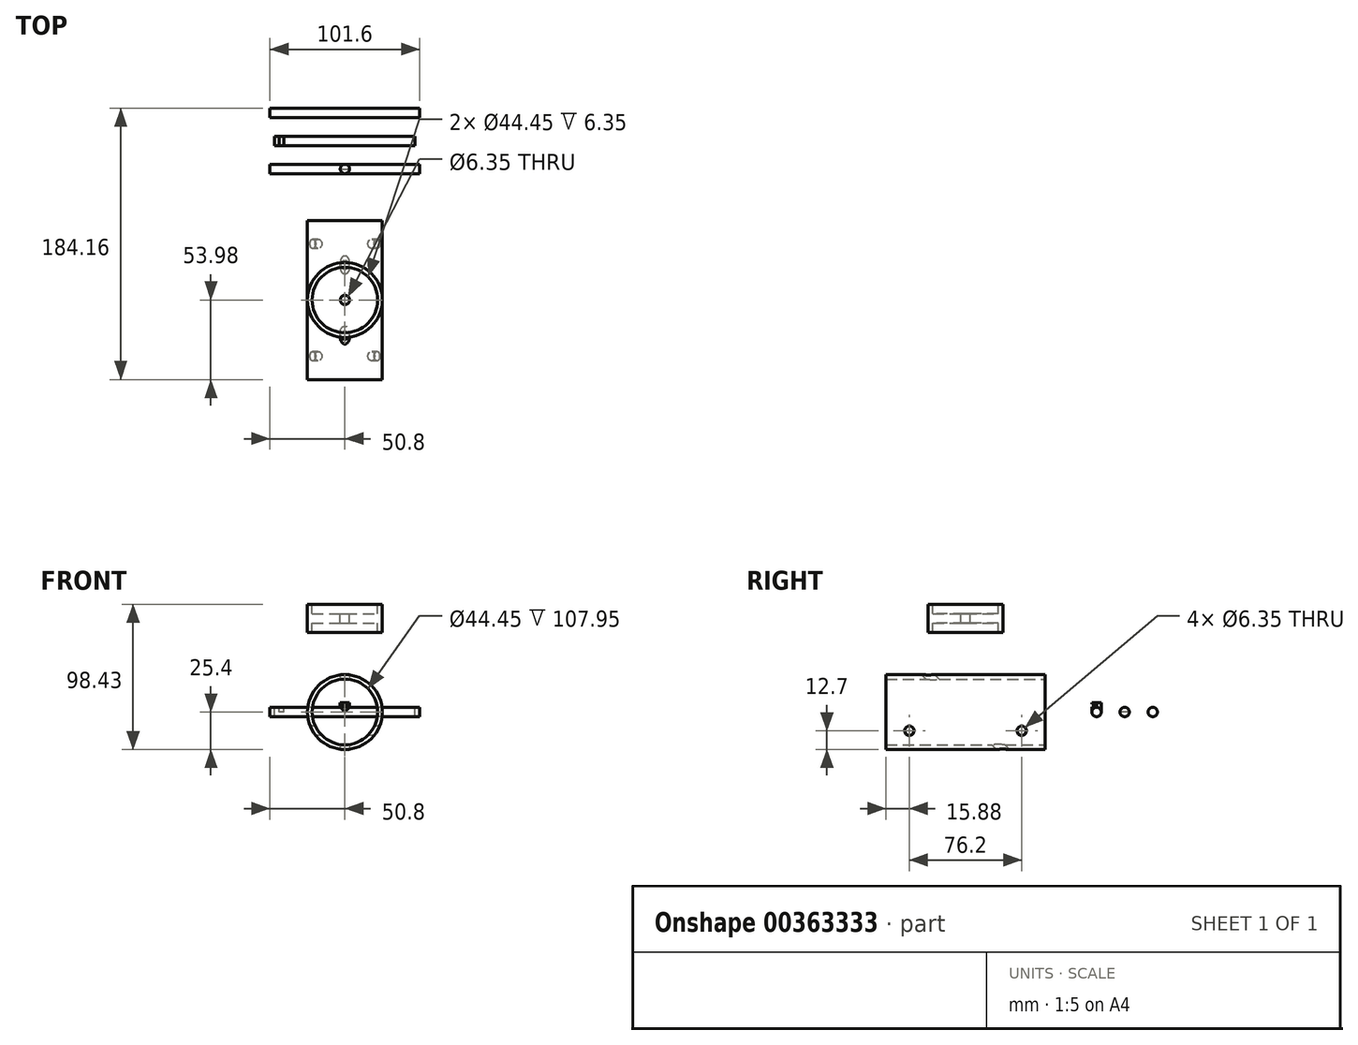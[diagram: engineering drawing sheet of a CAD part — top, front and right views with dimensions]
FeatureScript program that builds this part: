
annotation { "Feature Type Name" : "Feature", "Feature Type Description" : "" }
export const myFeature = defineFeature(function(context is Context, id is Id, definition is map)
    precondition{}
    {
        {
            var Q0;
            Q0=qCreatedBy(makeId("Front.planeOp"),FACE);
            var sketch = newSketch(context, id + "F0", { "sketchPlane" : qUnion([Q0])});
            skCircle(sketch, "E0", {"center": v(0, 0) * mm, "radius": 25.4 * mm});
            skCircle(sketch, "E1", {"center": v(0, 0) * mm, "radius": 22.23 * mm});
            skSolve(sketch);
        }
        {
            var Q0;
            Q0=makeQuery(id+"F0.imprint","IMPRINT",FACE,{"disambiguationData":[TD([[makeQuery(id+"F0.imprint","IMPRINT",EDGE,{"derivedFrom":sQuery(id+"F0.wireOp",EDGE,"E0")}),1.0]])]});
            var Q1;
            Q1=sQuery(id+"F0.wireOp",EDGE,"E0");
            extrude(context, id + "F1", {"entities" : qUnion([Q0]), "surfaceEntities" : qUnion([Q1]), "depth" : 107.95 * mm, "symmetric" : true});
        }
        {
            var Q0;
            Q0=qCreatedBy(makeId("Right.planeOp"),FACE);
            var sketch = newSketch(context, id + "F2", { "sketchPlane" : qUnion([Q0])});
            skLineSegment(sketch, "E2", {"start": v(0, 0) * mm, "end": v(-38.1, 0) * mm, "construction": true});
            skLineSegment(sketch, "E3", {"start": v(0, 0) * mm, "end": v(38.1, 0) * mm, "construction": true});
            skLineSegment(sketch, "E4", {"start": v(-38.1, 0) * mm, "end": v(-38.1, -12.7) * mm, "construction": true});
            skLineSegment(sketch, "E5", {"start": v(38.1, 0) * mm, "end": v(38.1, -12.7) * mm, "construction": true});
            skCircle(sketch, "E6", {"center": v(-38.1, -12.7) * mm, "radius": 3.18 * mm});
            skCircle(sketch, "E7", {"center": v(38.1, -12.7) * mm, "radius": 3.18 * mm});
            skSolve(sketch);
        }
        {
            var Q0;
            Q0=makeQuery(id+"F2.imprint","IMPRINT",FACE,{"disambiguationData":[TD([[makeQuery(id+"F2.imprint","IMPRINT",EDGE,{"derivedFrom":sQuery(id+"F2.wireOp",EDGE,"E6")}),1.0]])]});
            var Q1;
            Q1=makeQuery(id+"F2.imprint","IMPRINT",FACE,{"disambiguationData":[TD([[makeQuery(id+"F2.imprint","IMPRINT",EDGE,{"derivedFrom":sQuery(id+"F2.wireOp",EDGE,"E7")}),1.0]])]});
            extrude(context, id + "F3", {"entities" : qUnion([Q0, Q1]), "operationType" : NewBodyOperationType.REMOVE, "endBound" : BoundingType.THROUGH_ALL, "depth" : 25.4 * mm, "hasSecondDirection" : true, "secondDirectionBound" : BoundingType.THROUGH_ALL, "secondDirectionOppositeDirection" : true, "secondDirectionDepth" : 25.4 * mm});
        }
        {
            var Q0;
            Q0=qCreatedBy(makeId("Front.planeOp"),FACE);
            var sketch = newSketch(context, id + "F4", { "sketchPlane" : qUnion([Q0])});
            skLineSegment(sketch, "E8", {"start": v(-63.5, 0) * mm, "end": v(63.5, 0) * mm, "construction": true});
            skLineSegment(sketch, "E9", {"start": v(0, 63.5) * mm, "end": v(0, -63.5) * mm, "construction": true});
            skSolve(sketch);
        }
        {
            var Q0;
            Q0=sQuery(id+"F4.wireOp",EDGE,"E8");
            cPlane(context, id + "F5", {"entities" : qUnion([Q0]), "cplaneType" : CPlaneType.LINE_ANGLE, "offset" : 25.4 * mm, "angle" : 45 * degree, "oppositeDirection" : true, "width" : 152.4 * mm, "height" : 152.4 * mm});
        }
        {
            var Q0;
            Q0=qCreatedBy(id+"F5.planeOp",FACE);
            var sketch = newSketch(context, id + "F6", { "sketchPlane" : qUnion([Q0])});
            skCircle(sketch, "E10", {"center": v(0, 0) * mm, "radius": 3.18 * mm});
            skSolve(sketch);
        }
        {
            var Q0;
            Q0=makeQuery(id+"F6.imprint","IMPRINT",FACE,{"disambiguationData":[TD([[makeQuery(id+"F6.imprint","IMPRINT",EDGE,{"derivedFrom":sQuery(id+"F6.wireOp",EDGE,"E10")}),1.0]])]});
            extrude(context, id + "F7", {"entities" : qUnion([Q0]), "operationType" : NewBodyOperationType.REMOVE, "endBound" : BoundingType.THROUGH_ALL, "oppositeDirection" : true, "depth" : 25.4 * mm, "hasSecondDirection" : true, "secondDirectionBound" : BoundingType.THROUGH_ALL, "secondDirectionOppositeDirection" : false, "secondDirectionDepth" : 25.4 * mm});
        }
        {
            var Q0;
            Q0=qCreatedBy(makeId("Right.planeOp"),FACE);
            var sketch = newSketch(context, id + "F8", { "sketchPlane" : qUnion([Q0])});
            skLineSegment(sketch, "E11", {"start": v(0, 0) * mm, "end": v(127, 0) * mm, "construction": true});
            skCircle(sketch, "E12", {"center": v(127, 0) * mm, "radius": 3.18 * mm});
            skCircle(sketch, "E13", {"center": v(107.95, 0) * mm, "radius": 3.18 * mm});
            skCircle(sketch, "E14", {"center": v(88.9, 0) * mm, "radius": 3.18 * mm});
            skSolve(sketch);
        }
        {
            var Q0;
            Q0=makeQuery(id+"F8.imprint","IMPRINT",FACE,{"disambiguationData":[TD([[makeQuery(id+"F8.imprint","IMPRINT",EDGE,{"derivedFrom":sQuery(id+"F8.wireOp",EDGE,"E12")}),1.0]])]});
            var Q1;
            Q1=sQuery(id+"F8.wireOp",EDGE,"E12");
            extrude(context, id + "F9", {"entities" : qUnion([Q0]), "surfaceEntities" : qUnion([Q1]), "depth" : 101.6 * mm, "symmetric" : true});
        }
        {
            var Q0;
            Q0=makeQuery(id+"F8.imprint","IMPRINT",FACE,{"disambiguationData":[TD([[makeQuery(id+"F8.imprint","IMPRINT",EDGE,{"derivedFrom":sQuery(id+"F8.wireOp",EDGE,"E13")}),1.0]])]});
            extrude(context, id + "F10", {"entities" : qUnion([Q0]), "depth" : 95.25 * mm, "symmetric" : true});
        }
        {
            var Q0;
            Q0=makeQuery(id+"F10.opExtrude","CAP_FACE",FACE,{"disambiguationData":[OSD([sQuery(id+"F8.wireOp",EDGE,"E13")])],"isStart":true});
            var sketch = newSketch(context, id + "F11", { "sketchPlane" : qUnion([Q0])});
            skPoint(sketch, "E15", {"position": v(-107.95, 0) * mm});
            skLineSegment(sketch, "E16", {"start": v(-111.12, 0) * mm, "end": v(-104.78, 0) * mm});
            skLineSegment(sketch, "E17", {"start": v(-104.78, 0) * mm, "end": v(-104.78, 12.7) * mm});
            skLineSegment(sketch, "E18", {"start": v(-104.78, 12.7) * mm, "end": v(-111.12, 12.7) * mm});
            skLineSegment(sketch, "E19", {"start": v(-111.12, 12.7) * mm, "end": v(-111.12, 0) * mm});
            skSolve(sketch);
        }
        {
            var Q0;
            {var subQ0=sQuery(id+"F11.wireOp",EDGE,"E17");Q0=makeQuery(id+"F11.imprint","IMPRINT",FACE,{"disambiguationData":[TD([[makeQuery(id+"F11.imprint","IMPRINT",EDGE,{"derivedFrom":subQ0}),1.0]])]});}
            extrude(context, id + "F12", {"entities" : qUnion([Q0]), "operationType" : NewBodyOperationType.REMOVE, "oppositeDirection" : true, "depth" : 18.8 * mm, "hasSecondDirection" : true, "secondDirectionOppositeDirection" : true, "secondDirectionDepth" : 11.94 * mm});
        }
        {
            var Q0;
            Q0=makeQuery(id+"F10.opExtrude","CAP_FACE",FACE,{"disambiguationData":[OSD([sQuery(id+"F8.wireOp",EDGE,"E13")])],"isStart":true});
            var sketch = newSketch(context, id + "F13", { "sketchPlane" : qUnion([Q0])});
            skPoint(sketch, "E20", {"position": v(-107.95, 0) * mm});
            skLineSegment(sketch, "E21", {"start": v(-111.12, 0) * mm, "end": v(-104.78, 0) * mm});
            skLineSegment(sketch, "E22", {"start": v(-111.12, 0) * mm, "end": v(-111.12, 6.35) * mm});
            skLineSegment(sketch, "E23", {"start": v(-111.12, 6.35) * mm, "end": v(-104.78, 6.35) * mm});
            skLineSegment(sketch, "E24", {"start": v(-104.78, 6.35) * mm, "end": v(-104.78, 0) * mm});
            skSolve(sketch);
        }
        {
            var Q0;
            {var subQ0=sQuery(id+"F13.wireOp",EDGE,"E21");Q0=makeQuery(id+"F13.imprint","IMPRINT",FACE,{"disambiguationData":[TD([[makeQuery(id+"F13.imprint","IMPRINT",EDGE,{"derivedFrom":subQ0}),1.0]])]});}
            var Q1;
            {var subQ0=sQuery(id+"F13.wireOp",EDGE,"E22");Q1=makeQuery(id+"F13.imprint","IMPRINT",FACE,{"disambiguationData":[TD([[makeQuery(id+"F13.imprint","IMPRINT",EDGE,{"derivedFrom":subQ0}),-1.0]])]});}
            extrude(context, id + "F14", {"entities" : qUnion([Q0, Q1]), "operationType" : NewBodyOperationType.REMOVE, "oppositeDirection" : true, "depth" : 6.35 * mm, "hasSecondDirection" : true, "secondDirectionOppositeDirection" : true, "secondDirectionDepth" : 3.17 * mm});
        }
        {
            var Q0;
            Q0=makeQuery(id+"F8.imprint","IMPRINT",FACE,{"disambiguationData":[TD([[makeQuery(id+"F8.imprint","IMPRINT",EDGE,{"derivedFrom":sQuery(id+"F8.wireOp",EDGE,"E14")}),1.0]])]});
            extrude(context, id + "F15", {"entities" : qUnion([Q0]), "depth" : 101.6 * mm, "symmetric" : true});
        }
        {
            var Q0;
            Q0=qCreatedBy(makeId("Top.planeOp"),FACE);
            var sketch = newSketch(context, id + "F16", { "sketchPlane" : qUnion([Q0])});
            skPoint(sketch, "E25", {"position": v(0, 88.9) * mm});
            skCircle(sketch, "E26", {"center": v(0, 88.9) * mm, "radius": 3.18 * mm});
            skSolve(sketch);
        }
        {
            var Q0;
            Q0=qSketchRegion(id+"F16",true);
            extrude(context, id + "F17", {"entities" : qUnion([Q0]), "operationType" : NewBodyOperationType.ADD, "depth" : 6.35 * mm});
        }
        {
            var Q0;
            Q0=makeQuery(id+"F17.opExtrude","CAP_FACE",FACE,{"disambiguationData":[OSD([sQuery(id+"F16.wireOp",EDGE,"E26")])],"isStart":false});
            var sketch = newSketch(context, id + "F18", { "sketchPlane" : qUnion([Q0])});
            skLineSegment(sketch, "E27", {"start": v(0, 88.9) * mm, "end": v(3.18, 88.9) * mm});
            skLineSegment(sketch, "E28", {"start": v(3.18, 88.9) * mm, "end": v(3.18, 82.55) * mm});
            skLineSegment(sketch, "E29", {"start": v(3.18, 82.55) * mm, "end": v(-3.18, 82.55) * mm});
            skLineSegment(sketch, "E30", {"start": v(-3.18, 82.55) * mm, "end": v(-3.18, 88.9) * mm});
            skLineSegment(sketch, "E31", {"start": v(-3.18, 88.9) * mm, "end": v(0, 88.9) * mm});
            skSolve(sketch);
        }
        {
            var Q0;
            {var subQ0=sQuery(id+"F18.wireOp",EDGE,"E27");Q0=makeQuery(id+"F18.imprint","IMPRINT",FACE,{"disambiguationData":[TD([[makeQuery(id+"F18.imprint","IMPRINT",EDGE,{"derivedFrom":subQ0}),-1.0]])]});}
            extrude(context, id + "F19", {"entities" : qUnion([Q0]), "operationType" : NewBodyOperationType.REMOVE, "oppositeDirection" : true, "depth" : 2.8 * mm, "hasSecondDirection" : true, "secondDirectionOppositeDirection" : true, "secondDirectionDepth" : 1.02 * mm});
        }
        {
            var Q0;
            Q0=sQuery(id+"F4.wireOp",VERTEX,"E9.start");
            var Q1;
            Q1=sQuery(id+"F4.wireOp",EDGE,"E9");
            cPlane(context, id + "F20", {"entities" : qUnion([Q0, Q1]), "cplaneType" : CPlaneType.LINE_POINT, "offset" : 25.4 * mm, "width" : 152.4 * mm, "height" : 152.4 * mm});
        }
        {
            var Q0;
            Q0=qCreatedBy(id+"F20.planeOp",FACE);
            var sketch = newSketch(context, id + "F21", { "sketchPlane" : qUnion([Q0])});
            skPoint(sketch, "E32", {"position": v(0, 0) * mm});
            skCircle(sketch, "E33", {"center": v(0, 0) * mm, "radius": 25.4 * mm});
            skCircle(sketch, "E34", {"center": v(0, 0) * mm, "radius": 22.23 * mm});
            skCircle(sketch, "E35", {"center": v(0, 0) * mm, "radius": 3.18 * mm});
            skSolve(sketch);
        }
        {
            var Q0;
            Q0=qSketchRegion(id+"F21",true);
            extrude(context, id + "F22", {"entities" : qUnion([Q0]), "depth" : 19.05 * mm, "symmetric" : true});
        }
        {
            var Q0;
            Q0=makeQuery(id+"F21.imprint","IMPRINT",FACE,{"disambiguationData":[TD([[makeQuery(id+"F21.imprint","IMPRINT",EDGE,{"derivedFrom":sQuery(id+"F21.wireOp",EDGE,"E34")}),1.0]])]});
            extrude(context, id + "F23", {"entities" : qUnion([Q0]), "operationType" : NewBodyOperationType.ADD, "depth" : 6.35 * mm, "symmetric" : true});
        }
    });
